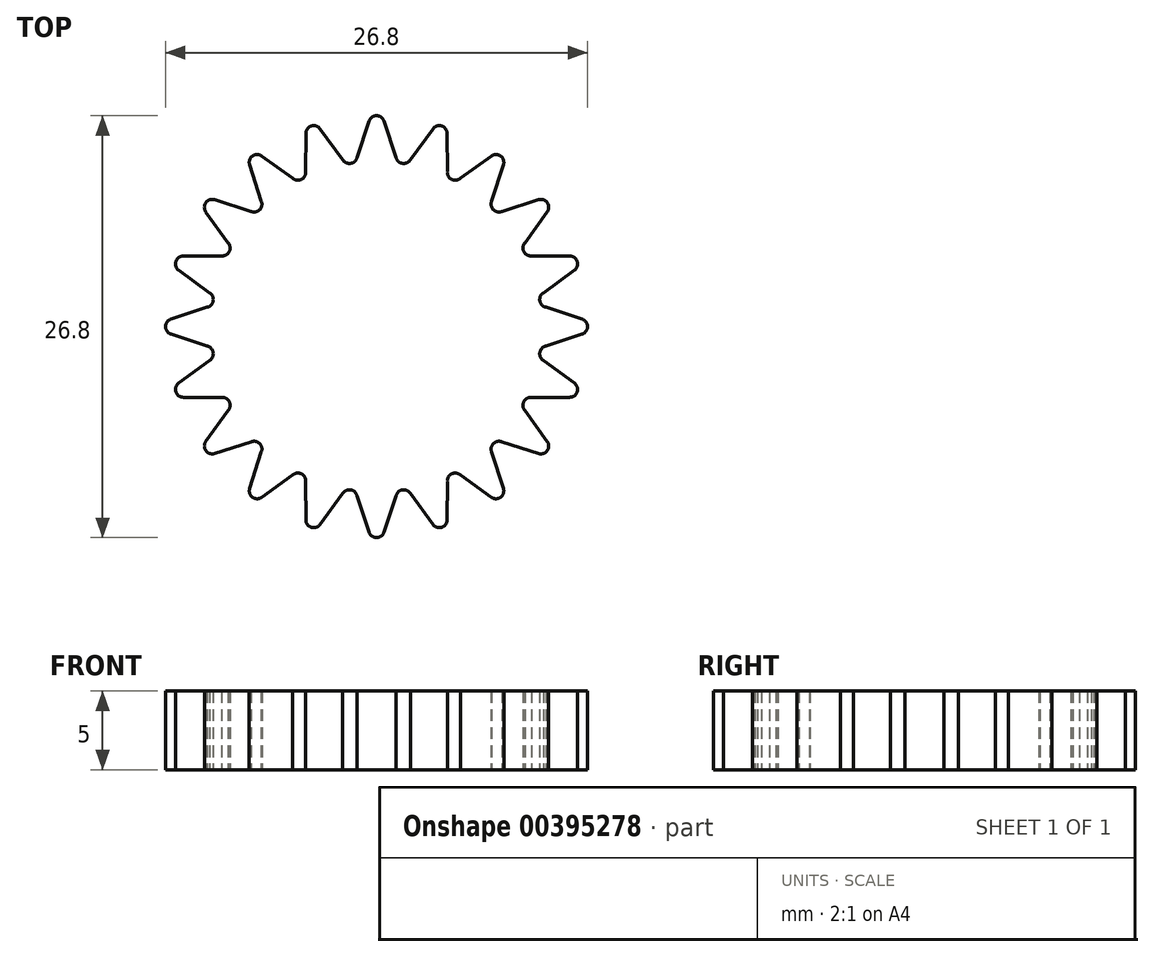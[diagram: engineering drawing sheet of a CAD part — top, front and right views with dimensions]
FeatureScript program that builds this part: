
annotation { "Feature Type Name" : "Feature", "Feature Type Description" : "" }
export const myFeature = defineFeature(function(context is Context, id is Id, definition is map)
    precondition{}
    {
        {
            var Q0;
            Q0=qCreatedBy(makeId("Top.planeOp"),FACE);
            var sketch = newSketch(context, id + "F0", { "sketchPlane" : qUnion([Q0])});
            skPoint(sketch, "E0", {"position": v(0, 11) * mm});
            skPoint(sketch, "E1", {"position": v(0, 12.9) * mm});
            skPoint(sketch, "E2", {"position": v(9.8, 5) * mm});
            skPoint(sketch, "E3", {"position": v(10.86, 1.72) * mm});
            skPoint(sketch, "E4", {"position": v(-7.78, 7.78) * mm});
            skPoint(sketch, "E5", {"position": v(-9.8, 5) * mm});
            skPoint(sketch, "E6", {"position": v(-10.86, 1.72) * mm});
            skPoint(sketch, "E7", {"position": v(-10.86, -1.72) * mm});
            skPoint(sketch, "E8", {"position": v(-9.8, -5) * mm});
            skPoint(sketch, "E9", {"position": v(-7.78, -7.78) * mm});
            skPoint(sketch, "E10", {"position": v(-5, -9.8) * mm});
            skPoint(sketch, "E11", {"position": v(-1.72, -10.86) * mm});
            skPoint(sketch, "E12", {"position": v(1.72, -10.86) * mm});
            skPoint(sketch, "E13", {"position": v(5, -9.8) * mm});
            skLineSegment(sketch, "E14", {"start": v(-1.23, 10.75) * mm, "end": v(-0.47, 13.06) * mm});
            skLineSegment(sketch, "E15.MirrorCS", {"start": v(1.23, 10.75) * mm, "end": v(0.47, 13.06) * mm});
            skArc(sketch, "E16", {"start": v(-0.47, 13.06) * mm, "mid": v(0, 13.4) * mm, "end": v(0.47, 13.06) * mm});
            skPoint(sketch, "E17", {"position": v(3.4, 10.46) * mm});
            skPoint(sketch, "E18", {"position": v(3.99, 12.27) * mm});
            skLineSegment(sketch, "E19", {"start": v(2.15, 10.6) * mm, "end": v(3.58, 12.56) * mm});
            skLineSegment(sketch, "E20.MirrorCS", {"start": v(4.5, 9.85) * mm, "end": v(4.49, 12.27) * mm});
            skArc(sketch, "E21", {"start": v(3.58, 12.56) * mm, "mid": v(4.14, 12.74) * mm, "end": v(4.49, 12.27) * mm});
            skArc(sketch, "E22", {"start": v(1.23, 10.75) * mm, "mid": v(1.64, 10.37) * mm, "end": v(2.15, 10.6) * mm});
            skArc(sketch, "E23.MirrorCS", {"start": v(-1.23, 10.75) * mm, "mid": v(-1.64, 10.37) * mm, "end": v(-2.15, 10.6) * mm});
            skPoint(sketch, "E24", {"position": v(6.47, 8.9) * mm});
            skPoint(sketch, "E25", {"position": v(7.58, 10.44) * mm});
            skPoint(sketch, "E26", {"position": v(7.78, 7.78) * mm});
            skLineSegment(sketch, "E27", {"start": v(5.32, 9.42) * mm, "end": v(7.3, 10.84) * mm});
            skLineSegment(sketch, "E28.MirrorCS", {"start": v(7.32, 7.97) * mm, "end": v(8.06, 10.28) * mm});
            skArc(sketch, "E29", {"start": v(7.3, 10.84) * mm, "mid": v(7.88, 10.84) * mm, "end": v(8.06, 10.28) * mm});
            skPoint(sketch, "E30", {"position": v(8.9, 6.47) * mm});
            skPoint(sketch, "E31", {"position": v(10.44, 7.58) * mm});
            skLineSegment(sketch, "E32", {"start": v(7.97, 7.32) * mm, "end": v(10.28, 8.06) * mm});
            skLineSegment(sketch, "E33.MirrorCS", {"start": v(9.42, 5.32) * mm, "end": v(10.84, 7.3) * mm});
            skArc(sketch, "E34", {"start": v(10.28, 8.06) * mm, "mid": v(10.84, 7.88) * mm, "end": v(10.84, 7.3) * mm});
            skArc(sketch, "E35", {"start": v(7.32, 7.97) * mm, "mid": v(7.42, 7.42) * mm, "end": v(7.97, 7.32) * mm});
            skArc(sketch, "E36.MirrorCS", {"start": v(5.32, 9.42) * mm, "mid": v(4.77, 9.36) * mm, "end": v(4.5, 9.85) * mm});
            skPoint(sketch, "E37", {"position": v(10.46, 3.4) * mm});
            skPoint(sketch, "E38", {"position": v(12.27, 3.99) * mm});
            skPoint(sketch, "E39", {"position": v(7.78, -7.78) * mm});
            skLineSegment(sketch, "E40", {"start": v(9.85, 4.5) * mm, "end": v(12.27, 4.49) * mm});
            skLineSegment(sketch, "E41.MirrorCS", {"start": v(10.6, 2.15) * mm, "end": v(12.56, 3.58) * mm});
            skArc(sketch, "E42", {"start": v(12.27, 4.49) * mm, "mid": v(12.74, 4.14) * mm, "end": v(12.56, 3.58) * mm});
            skPoint(sketch, "E43", {"position": v(12.9, 0) * mm});
            skLineSegment(sketch, "E44", {"start": v(10.75, 1.23) * mm, "end": v(13.06, 0.47) * mm});
            skArc(sketch, "E45", {"start": v(13.06, 0.47) * mm, "mid": v(13.4, 0) * mm, "end": v(13.06, -0.47) * mm});
            skArc(sketch, "E46", {"start": v(10.6, 2.15) * mm, "mid": v(10.37, 1.64) * mm, "end": v(10.75, 1.23) * mm});
            skArc(sketch, "E47.MirrorCS", {"start": v(9.85, 4.5) * mm, "mid": v(9.36, 4.77) * mm, "end": v(9.42, 5.32) * mm});
            skArc(sketch, "E48.MirrorCS", {"start": v(-10.28, 8.06) * mm, "mid": v(-10.84, 7.88) * mm, "end": v(-10.84, 7.3) * mm});
            skArc(sketch, "E49.MirrorCS", {"start": v(-13.06, 0.47) * mm, "mid": v(-13.4, 0) * mm, "end": v(-13.06, -0.47) * mm});
            skPoint(sketch, "E50.MirrorP", {"position": v(-5, 9.8) * mm});
            skArc(sketch, "E51.MirrorCS", {"start": v(-12.27, 4.49) * mm, "mid": v(-12.74, 4.14) * mm, "end": v(-12.56, 3.58) * mm});
            skPoint(sketch, "E52.MirrorP", {"position": v(-3.99, 12.27) * mm});
            skPoint(sketch, "E53.MirrorP", {"position": v(-7.58, 10.44) * mm});
            skLineSegment(sketch, "E54.MirrorCS", {"start": v(-10.6, 2.15) * mm, "end": v(-12.56, 3.58) * mm});
            skArc(sketch, "E55.MirrorCS", {"start": v(-7.3, 10.84) * mm, "mid": v(-7.88, 10.84) * mm, "end": v(-8.06, 10.28) * mm});
            skPoint(sketch, "E56.MirrorP", {"position": v(-8.9, 6.47) * mm});
            skLineSegment(sketch, "E57.MirrorCS", {"start": v(-2.15, 10.6) * mm, "end": v(-3.58, 12.56) * mm});
            skLineSegment(sketch, "E58.MirrorCS", {"start": v(-10.75, 1.23) * mm, "end": v(-13.06, 0.47) * mm});
            skArc(sketch, "E59.MirrorCS", {"start": v(-5.32, 9.42) * mm, "mid": v(-4.77, 9.36) * mm, "end": v(-4.5, 9.85) * mm});
            skArc(sketch, "E60.MirrorCS", {"start": v(-3.58, 12.56) * mm, "mid": v(-4.14, 12.74) * mm, "end": v(-4.49, 12.27) * mm});
            skPoint(sketch, "E61.MirrorP", {"position": v(-3.4, 10.46) * mm});
            skArc(sketch, "E62.MirrorCS", {"start": v(-9.85, 4.5) * mm, "mid": v(-9.36, 4.77) * mm, "end": v(-9.42, 5.32) * mm});
            skPoint(sketch, "E63.MirrorP", {"position": v(-6.47, 8.9) * mm});
            skLineSegment(sketch, "E64.MirrorCS", {"start": v(-5.32, 9.42) * mm, "end": v(-7.3, 10.84) * mm});
            skLineSegment(sketch, "E65.MirrorCS", {"start": v(-9.42, 5.32) * mm, "end": v(-10.84, 7.3) * mm});
            skLineSegment(sketch, "E66.MirrorCS", {"start": v(-7.97, 7.32) * mm, "end": v(-10.28, 8.06) * mm});
            skLineSegment(sketch, "E67.MirrorCS", {"start": v(-9.85, 4.5) * mm, "end": v(-12.27, 4.49) * mm});
            skLineSegment(sketch, "E68.MirrorCS", {"start": v(-7.32, 7.97) * mm, "end": v(-8.06, 10.28) * mm});
            skArc(sketch, "E69.MirrorCS", {"start": v(-10.6, 2.15) * mm, "mid": v(-10.37, 1.64) * mm, "end": v(-10.75, 1.23) * mm});
            skArc(sketch, "E70.MirrorCS", {"start": v(-7.32, 7.97) * mm, "mid": v(-7.42, 7.42) * mm, "end": v(-7.97, 7.32) * mm});
            skPoint(sketch, "E71.MirrorP", {"position": v(-10.46, 3.4) * mm});
            skLineSegment(sketch, "E72.MirrorCS", {"start": v(-4.5, 9.85) * mm, "end": v(-4.49, 12.27) * mm});
            skArc(sketch, "E73.MirrorCS", {"start": v(-5.32, -9.42) * mm, "mid": v(-4.77, -9.36) * mm, "end": v(-4.5, -9.85) * mm});
            skArc(sketch, "E74.MirrorCS", {"start": v(5.32, -9.42) * mm, "mid": v(4.77, -9.36) * mm, "end": v(4.5, -9.85) * mm});
            skArc(sketch, "E75.MirrorCS", {"start": v(-9.85, -4.5) * mm, "mid": v(-9.36, -4.77) * mm, "end": v(-9.42, -5.32) * mm});
            skPoint(sketch, "E76.MirrorP", {"position": v(10.86, -1.72) * mm});
            skArc(sketch, "E77.MirrorCS", {"start": v(-7.32, -7.97) * mm, "mid": v(-7.42, -7.42) * mm, "end": v(-7.97, -7.32) * mm});
            skArc(sketch, "E78.MirrorCS", {"start": v(10.28, -8.06) * mm, "mid": v(10.84, -7.88) * mm, "end": v(10.84, -7.3) * mm});
            skLineSegment(sketch, "E79.MirrorCS", {"start": v(-1.23, -10.75) * mm, "end": v(-0.47, -13.06) * mm});
            skArc(sketch, "E80.MirrorCS", {"start": v(13.06, -0.47) * mm, "mid": v(13.4, 0) * mm, "end": v(13.06, 0.47) * mm});
            skArc(sketch, "E81.MirrorCS", {"start": v(-1.23, -10.75) * mm, "mid": v(-1.64, -10.37) * mm, "end": v(-2.15, -10.6) * mm});
            skPoint(sketch, "E82.MirrorP", {"position": v(0, -12.9) * mm});
            skPoint(sketch, "E83.MirrorP", {"position": v(9.8, -5) * mm});
            skPoint(sketch, "E84.MirrorP", {"position": v(0, -11) * mm});
            skArc(sketch, "E85.MirrorCS", {"start": v(12.27, -4.49) * mm, "mid": v(12.74, -4.14) * mm, "end": v(12.56, -3.58) * mm});
            skLineSegment(sketch, "E86.MirrorCS", {"start": v(-2.15, -10.6) * mm, "end": v(-3.58, -12.56) * mm});
            skLineSegment(sketch, "E87.MirrorCS", {"start": v(4.5, -9.85) * mm, "end": v(4.49, -12.27) * mm});
            skLineSegment(sketch, "E88.MirrorCS", {"start": v(-9.42, -5.32) * mm, "end": v(-10.84, -7.3) * mm});
            skPoint(sketch, "E89.MirrorP", {"position": v(-12.27, -3.99) * mm});
            skLineSegment(sketch, "E90.MirrorCS", {"start": v(9.42, -5.32) * mm, "end": v(10.84, -7.3) * mm});
            skLineSegment(sketch, "E91.MirrorCS", {"start": v(-7.32, -7.97) * mm, "end": v(-8.06, -10.28) * mm});
            skPoint(sketch, "E92.MirrorP", {"position": v(-10.46, -3.4) * mm});
            skArc(sketch, "E93.MirrorCS", {"start": v(-13.06, -0.47) * mm, "mid": v(-13.4, 0) * mm, "end": v(-13.06, 0.47) * mm});
            skArc(sketch, "E94.MirrorCS", {"start": v(-0.47, -13.06) * mm, "mid": v(0, -13.4) * mm, "end": v(0.47, -13.06) * mm});
            skPoint(sketch, "E95.MirrorP", {"position": v(7.58, -10.44) * mm});
            skLineSegment(sketch, "E96.MirrorCS", {"start": v(7.97, -7.32) * mm, "end": v(10.28, -8.06) * mm});
            skArc(sketch, "E97.MirrorCS", {"start": v(7.3, -10.84) * mm, "mid": v(7.88, -10.84) * mm, "end": v(8.06, -10.28) * mm});
            skPoint(sketch, "E98.MirrorP", {"position": v(-3.4, -10.46) * mm});
            skLineSegment(sketch, "E99.MirrorCS", {"start": v(10.6, -2.15) * mm, "end": v(12.56, -3.58) * mm});
            skLineSegment(sketch, "E100.MirrorCS", {"start": v(5.32, -9.42) * mm, "end": v(7.3, -10.84) * mm});
            skArc(sketch, "E101.MirrorCS", {"start": v(-10.6, -2.15) * mm, "mid": v(-10.37, -1.64) * mm, "end": v(-10.75, -1.23) * mm});
            skPoint(sketch, "E102.MirrorP", {"position": v(6.47, -8.9) * mm});
            skPoint(sketch, "E103.MirrorP", {"position": v(3.99, -12.27) * mm});
            skLineSegment(sketch, "E104.MirrorCS", {"start": v(7.32, -7.97) * mm, "end": v(8.06, -10.28) * mm});
            skLineSegment(sketch, "E105.MirrorCS", {"start": v(-9.85, -4.5) * mm, "end": v(-12.27, -4.49) * mm});
            skLineSegment(sketch, "E106.MirrorCS", {"start": v(-10.6, -2.15) * mm, "end": v(-12.56, -3.58) * mm});
            skArc(sketch, "E107.MirrorCS", {"start": v(3.58, -12.56) * mm, "mid": v(4.14, -12.74) * mm, "end": v(4.49, -12.27) * mm});
            skArc(sketch, "E108.MirrorCS", {"start": v(9.85, -4.5) * mm, "mid": v(9.36, -4.77) * mm, "end": v(9.42, -5.32) * mm});
            skLineSegment(sketch, "E109.MirrorCS", {"start": v(-7.97, -7.32) * mm, "end": v(-10.28, -8.06) * mm});
            skLineSegment(sketch, "E110.MirrorCS", {"start": v(9.85, -4.5) * mm, "end": v(12.27, -4.49) * mm});
            skArc(sketch, "E111.MirrorCS", {"start": v(-12.27, -4.49) * mm, "mid": v(-12.74, -4.14) * mm, "end": v(-12.56, -3.58) * mm});
            skArc(sketch, "E112.MirrorCS", {"start": v(1.23, -10.75) * mm, "mid": v(1.64, -10.37) * mm, "end": v(2.15, -10.6) * mm});
            skLineSegment(sketch, "E113.MirrorCS", {"start": v(-5.32, -9.42) * mm, "end": v(-7.3, -10.84) * mm});
            skLineSegment(sketch, "E114.MirrorCS", {"start": v(2.15, -10.6) * mm, "end": v(3.58, -12.56) * mm});
            skArc(sketch, "E115.MirrorCS", {"start": v(10.6, -2.15) * mm, "mid": v(10.37, -1.64) * mm, "end": v(10.75, -1.23) * mm});
            skLineSegment(sketch, "E116.MirrorCS", {"start": v(-10.75, -1.23) * mm, "end": v(-13.06, -0.47) * mm});
            skPoint(sketch, "E117.MirrorP", {"position": v(8.9, -6.47) * mm});
            skLineSegment(sketch, "E118.MirrorCS", {"start": v(1.23, -10.75) * mm, "end": v(0.47, -13.06) * mm});
            skPoint(sketch, "E119.MirrorP", {"position": v(-7.58, -10.44) * mm});
            skPoint(sketch, "E120.MirrorP", {"position": v(-6.47, -8.9) * mm});
            skArc(sketch, "E121.MirrorCS", {"start": v(-7.3, -10.84) * mm, "mid": v(-7.88, -10.84) * mm, "end": v(-8.06, -10.28) * mm});
            skPoint(sketch, "E122.MirrorP", {"position": v(-8.9, -6.47) * mm});
            skArc(sketch, "E123.MirrorCS", {"start": v(7.32, -7.97) * mm, "mid": v(7.42, -7.42) * mm, "end": v(7.97, -7.32) * mm});
            skPoint(sketch, "E124.MirrorP", {"position": v(-3.99, -12.27) * mm});
            skPoint(sketch, "E125.MirrorP", {"position": v(10.46, -3.4) * mm});
            skPoint(sketch, "E126.MirrorP", {"position": v(3.4, -10.46) * mm});
            skArc(sketch, "E127.MirrorCS", {"start": v(-10.28, -8.06) * mm, "mid": v(-10.84, -7.88) * mm, "end": v(-10.84, -7.3) * mm});
            skLineSegment(sketch, "E128.MirrorCS", {"start": v(10.75, -1.23) * mm, "end": v(13.06, -0.47) * mm});
            skArc(sketch, "E129.MirrorCS", {"start": v(-3.58, -12.56) * mm, "mid": v(-4.14, -12.74) * mm, "end": v(-4.49, -12.27) * mm});
            skLineSegment(sketch, "E130.MirrorCS", {"start": v(-4.5, -9.85) * mm, "end": v(-4.49, -12.27) * mm});
            skSolve(sketch);
        }
        {
            var Q0;
            Q0 = qSketchRegion(id + "F0", true);
            var Q1;
            Q1=makeQuery(id+"F0.imprint","IMPRINT",FACE,{"disambiguationData":[TD([[makeQuery(id+"F0.imprint","IMPRINT",EDGE,{"derivedFrom":sQuery(id+"F0.wireOp",EDGE,"E15.MirrorCS")}),1.0]])]});
            extrude(context, id + "F1", {"entities" : qUnion([Q0, Q1]), "depth" : 5 * mm});
        }
    });
